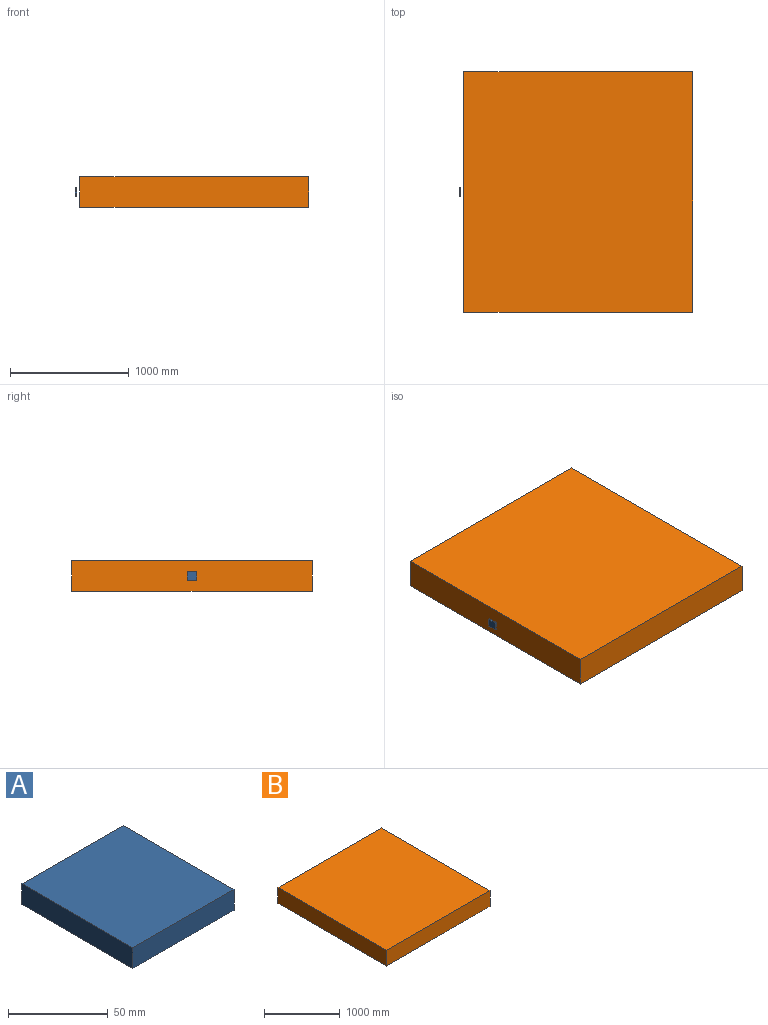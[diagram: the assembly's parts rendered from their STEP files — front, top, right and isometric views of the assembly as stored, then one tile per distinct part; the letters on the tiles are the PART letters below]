
ASSEMBLY  parts=2 mates=1
PART A: 6 faces, bbox 71.6x78.6x12.7 mm
  f0: plane 78.64x12.7mm, normal (-1,0,0), area 998.7mm2, adj f1,f3,f4,f5
  f1: plane 71.6x12.7mm, normal (0,-1,0), area 909.3mm2, adj f0,f2,f4,f5
  f2: plane 78.64x12.7mm, normal (1,0,0), area 998.7mm2, adj f1,f3,f4,f5
  f3: plane 71.6x12.7mm, normal (0,1,0), area 909.3mm2, adj f0,f2,f4,f5
  f4: plane 78.64x71.6mm, normal (0,0,1), area 5630.6mm2, adj f0,f1,f2,f3
  f5: plane 78.64x71.6mm, normal (0,0,-1), area 5630.6mm2, adj f0,f1,f2,f3
PART B: 6 faces, bbox 1930.4x2032x254 mm
  f0: plane 2032x254mm, normal (-1,0,0), area 516128mm2, adj f1,f3,f4,f5
  f1: plane 1930.4x254mm, normal (0,-1,0), area 490321.6mm2, adj f0,f2,f4,f5
  f2: plane 2032x254mm, normal (1,0,0), area 516128mm2, adj f1,f3,f4,f5
  f3: plane 1930.4x254mm, normal (0,1,0), area 490321.6mm2, adj f0,f2,f4,f5
  f4: plane 2032x1930.4mm, normal (0,0,1), area 3922572.8mm2, adj f0,f1,f2,f3
  f5: plane 2032x1930.4mm, normal (0,0,-1), area 3922572.8mm2, adj f0,f1,f2,f3
PLACE A rot(axis=(0,1,0),90deg) t=(100.09,678.28,342.32)mm
PLACE B t=(138.19,-298.4,179.53)mm
MATE parallel A.f4 <-> B.f0  axis (1,0,0) through (112.79,717.6,306.53)mm
